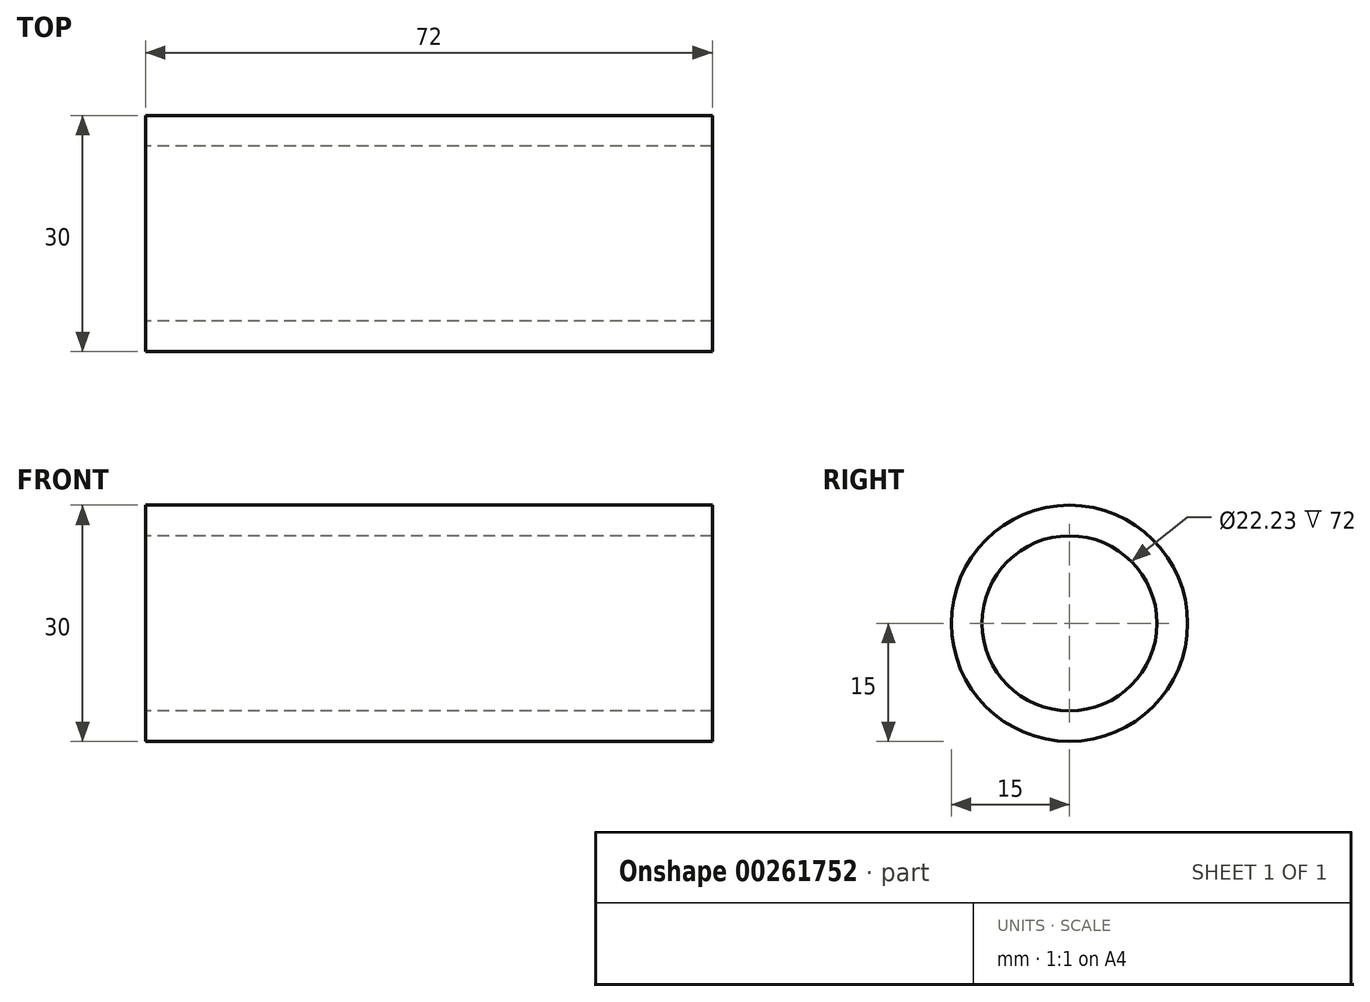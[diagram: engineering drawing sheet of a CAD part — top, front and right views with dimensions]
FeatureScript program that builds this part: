
annotation { "Feature Type Name" : "Feature", "Feature Type Description" : "" }
export const myFeature = defineFeature(function(context is Context, id is Id, definition is map)
    precondition{}
    {
        {
            var Q0;
            Q0=qCreatedBy(makeId("Front.planeOp"),FACE);
            var sketch = newSketch(context, id + "F0", { "sketchPlane" : qUnion([Q0])});
            skLineSegment(sketch, "E0", {"start": v(0, 15) * mm, "end": v(36, 15) * mm});
            skLineSegment(sketch, "E1", {"start": v(36, 15) * mm, "end": v(36, 11.12) * mm});
            skLineSegment(sketch, "E2", {"start": v(36, 11.12) * mm, "end": v(0, 11.12) * mm});
            skLineSegment(sketch, "E3.MirrorCS", {"start": v(0, 15) * mm, "end": v(-36, 15) * mm});
            skLineSegment(sketch, "E4.MirrorCS", {"start": v(-36, 11.12) * mm, "end": v(0, 11.12) * mm});
            skLineSegment(sketch, "E5.MirrorCS", {"start": v(-36, 15) * mm, "end": v(-36, 11.12) * mm});
            skLineSegment(sketch, "E6", {"start": v(-45.55, 0) * mm, "end": v(62.07, 0) * mm, "construction": true});
            skSolve(sketch);
        }
        {
            var Q0;
            Q0=makeQuery(id+"F0.imprint","IMPRINT",FACE,{"disambiguationData":[TD([[makeQuery(id+"F0.imprint","IMPRINT",EDGE,{"derivedFrom":sQuery(id+"F0.wireOp",EDGE,"E0")}),-1.0]])]});
            var Q1;
            Q1=sQuery(id+"F0.wireOp",EDGE,"E6");
            revolve(context, id + "F1", {"entities" : qUnion([Q0]), "axis" : qUnion([Q1]), "revolveType" : RevolveType.FULL});
        }
    });
